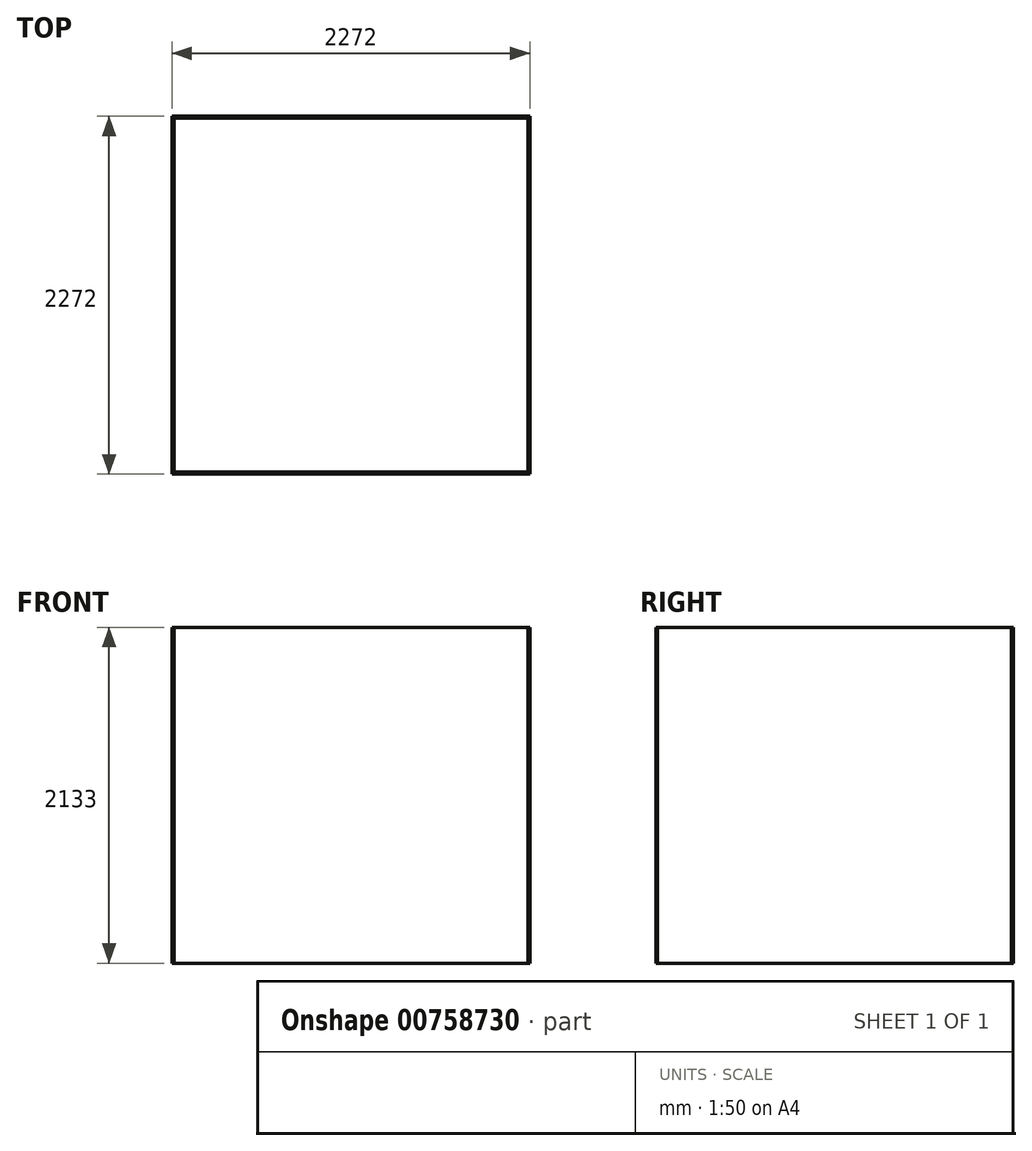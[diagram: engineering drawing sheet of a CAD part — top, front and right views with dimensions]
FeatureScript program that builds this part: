
annotation { "Feature Type Name" : "Feature", "Feature Type Description" : "" }
export const myFeature = defineFeature(function(context is Context, id is Id, definition is map)
    precondition{}
    {
        {
            var Q0;
            Q0=qCreatedBy(makeId("Top.planeOp"),FACE);
            var sketch = newSketch(context, id + "F0", { "sketchPlane" : qUnion([Q0])});
            skLineSegment(sketch, "E0.bottom", {"start": v(1124, 1124) * mm, "end": v(-1124, 1124) * mm});
            skLineSegment(sketch, "E0.top", {"start": v(1124, -1124) * mm, "end": v(-1124, -1124) * mm});
            skLineSegment(sketch, "E0.left", {"start": v(1124, 1124) * mm, "end": v(1124, -1124) * mm});
            skLineSegment(sketch, "E0.right", {"start": v(-1124, 1124) * mm, "end": v(-1124, -1124) * mm});
            skPoint(sketch, "E0.middle", {"position": v(0, 0) * mm});
            skSolve(sketch);
        }
        {
            var Q0;
            Q0=makeQuery(id+"F0.imprint","IMPRINT",FACE,{"disambiguationData":[TD([[makeQuery(id+"F0.imprint","IMPRINT",EDGE,{"derivedFrom":sQuery(id+"F0.wireOp",EDGE,"E0.bottom")}),1.0]])]});
            var sketch = newSketch(context, id + "F1", { "sketchPlane" : qUnion([Q0])});
            skLineSegment(sketch, "E1.bottom", {"start": v(-1054, -1054) * mm, "end": v(1054, -1054) * mm});
            skLineSegment(sketch, "E1.top", {"start": v(-1054, 1054) * mm, "end": v(1054, 1054) * mm});
            skLineSegment(sketch, "E1.left", {"start": v(-1054, -1054) * mm, "end": v(-1054, 1054) * mm});
            skLineSegment(sketch, "E1.right", {"start": v(1054, -1054) * mm, "end": v(1054, 1054) * mm});
            skPoint(sketch, "E1.middle", {"position": v(0, 0) * mm});
            skSolve(sketch);
        }
        {
            var Q0;
            Q0 = qSketchRegion(id + "F0", true);
            var Q1;
            Q1=sQuery(id+"F0.wireOp",EDGE,"E0.right");
            var Q2;
            Q2=sQuery(id+"F1.wireOp",EDGE,"E1.left");
            var Q3;
            Q3=sQuery(id+"F1.wireOp",EDGE,"E1.bottom");
            var Q4;
            Q4=sQuery(id+"F0.wireOp",EDGE,"E0.top");
            var Q5;
            Q5=sQuery(id+"F1.wireOp",EDGE,"E1.right");
            var Q6;
            Q6=sQuery(id+"F0.wireOp",EDGE,"E0.left");
            var Q7;
            Q7=sQuery(id+"F0.wireOp",EDGE,"E0.bottom");
            var Q8;
            Q8=sQuery(id+"F1.wireOp",EDGE,"E1.top");
            extrude(context, id + "F2", {"entities" : qUnion([Q0]), "bodyType" : ToolBodyType.SURFACE, "surfaceEntities" : qUnion([Q1, Q2, Q3, Q4, Q5, Q6, Q7, Q8]), "oppositeDirection" : true, "depth" : 2133 * mm, "offsetDistance" : 25 * mm});
        }
        {
            var Q0;
            Q0=makeQuery(id+"F2.opExtrude","SWEPT_FACE",FACE,{"disambiguationData":[OSD([sQuery(id+"F0.wireOp",EDGE,"E0.top")])]});
            extrude(context, id + "F3", {"entities" : qUnion([Q0]), "oppositeDirection" : true, "depth" : 12 * mm, "offsetDistance" : 25 * mm});
        }
        {
            var Q0;
            Q0=makeQuery(id+"F2.opExtrude","SWEPT_FACE",FACE,{"disambiguationData":[OSD([sQuery(id+"F0.wireOp",EDGE,"E0.left")])]});
            extrude(context, id + "F4", {"entities" : qUnion([Q0]), "operationType" : NewBodyOperationType.ADD, "oppositeDirection" : true, "depth" : 12 * mm, "offsetDistance" : 25 * mm});
        }
        {
            var Q0;
            Q0=makeQuery(id+"F2.opExtrude","SWEPT_FACE",FACE,{"disambiguationData":[OSD([sQuery(id+"F0.wireOp",EDGE,"E0.bottom")])]});
            extrude(context, id + "F5", {"entities" : qUnion([Q0]), "operationType" : NewBodyOperationType.ADD, "oppositeDirection" : true, "depth" : 12 * mm, "offsetDistance" : 25 * mm});
        }
        {
            var Q0;
            Q0=makeQuery(id+"F2.opExtrude","SWEPT_FACE",FACE,{"disambiguationData":[OSD([sQuery(id+"F0.wireOp",EDGE,"E0.right")])]});
            extrude(context, id + "F6", {"entities" : qUnion([Q0]), "oppositeDirection" : true, "depth" : 12 * mm, "offsetDistance" : 25 * mm});
        }
        {
            var Q0;
            Q0=makeQuery(id+"F6.opExtrude","SWEPT_FACE",FACE,{"disambiguationData":[OSD([sQuery(id+"F0.wireOp",VERTEX,"E0.top.end")])]});
            extrude(context, id + "F7", {"entities" : qUnion([Q0]), "depth" : 12 * mm, "offsetDistance" : 25 * mm});
        }
        {
            var Q0;
            Q0=makeQuery(id+"F5.opExtrude","SWEPT_FACE",FACE,{"disambiguationData":[OSD([sQuery(id+"F0.wireOp",VERTEX,"E0.bottom.end")])]});
            extrude(context, id + "F8", {"entities" : qUnion([Q0]), "depth" : 12 * mm, "offsetDistance" : 25 * mm});
        }
        {
            var Q0;
            Q0=makeQuery(id+"F5.opExtrude","SWEPT_FACE",FACE,{"disambiguationData":[OSD([sQuery(id+"F0.wireOp",VERTEX,"E0.bottom.start")])]});
            extrude(context, id + "F9", {"entities" : qUnion([Q0]), "depth" : 12 * mm, "offsetDistance" : 25 * mm});
        }
        {
            var Q0;
            Q0=makeQuery(id+"F4.opExtrude","SWEPT_FACE",FACE,{"disambiguationData":[OSD([sQuery(id+"F0.wireOp",VERTEX,"E0.left.end")])]});
            extrude(context, id + "F10", {"entities" : qUnion([Q0]), "depth" : 12 * mm, "offsetDistance" : 25 * mm});
        }
    });
